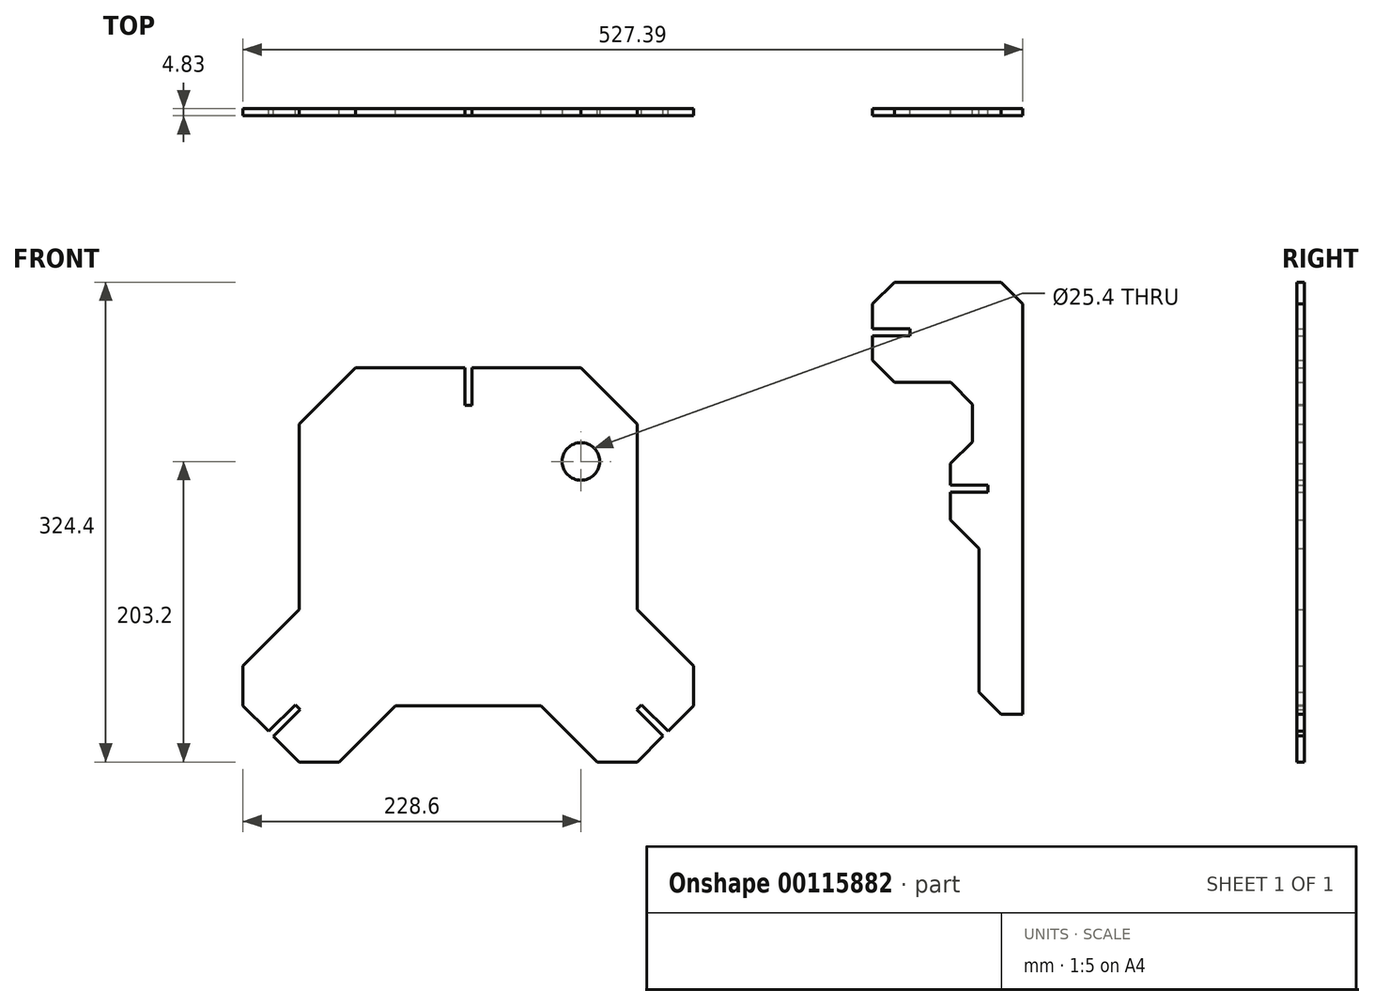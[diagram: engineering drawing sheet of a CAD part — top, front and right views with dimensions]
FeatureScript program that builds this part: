
annotation { "Feature Type Name" : "Feature", "Feature Type Description" : "" }
export const myFeature = defineFeature(function(context is Context, id is Id, definition is map)
    precondition{}
    {
        {
            var Q0;
            Q0=qCreatedBy(makeId("Front.planeOp"),FACE);
            var sketch = newSketch(context, id + "F0", { "sketchPlane" : qUnion([Q0])});
            skLineSegment(sketch, "E0.bottom", {"start": v(76.2, 133.35) * mm, "end": v(-76.2, 133.35) * mm});
            skLineSegment(sketch, "E0.top", {"start": v(114.3, -133.35) * mm, "end": v(87.36, -133.35) * mm});
            skLineSegment(sketch, "E0.left", {"start": v(114.3, 95.25) * mm, "end": v(114.3, -30.2) * mm});
            skLineSegment(sketch, "E0.right", {"start": v(-114.3, 95.25) * mm, "end": v(-114.3, -30.2) * mm});
            skPoint(sketch, "E0.middle", {"position": v(0, 0) * mm});
            skLineSegment(sketch, "E1", {"start": v(-76.2, 133.35) * mm, "end": v(-114.3, 95.25) * mm});
            skPoint(sketch, "E2.orphan", {"position": v(-114.3, 133.35) * mm});
            skLineSegment(sketch, "E3", {"start": v(76.2, 133.35) * mm, "end": v(114.3, 95.25) * mm});
            skPoint(sketch, "E4.orphan", {"position": v(114.3, 133.35) * mm});
            skLineSegment(sketch, "E5", {"start": v(114.3, -133.35) * mm, "end": v(152.4, -95.25) * mm});
            skLineSegment(sketch, "E6", {"start": v(152.4, -95.25) * mm, "end": v(152.4, -68.3) * mm});
            skLineSegment(sketch, "E7", {"start": v(152.4, -68.3) * mm, "end": v(114.3, -30.2) * mm});
            skLineSegment(sketch, "E8", {"start": v(87.36, -133.35) * mm, "end": v(49.26, -95.25) * mm});
            skPoint(sketch, "E9.orphan", {"position": v(-114.3, -133.35) * mm});
            skLineSegment(sketch, "E10", {"start": v(152.4, -68.3) * mm, "end": v(152.4, -95.25) * mm});
            skLineSegment(sketch, "E11.MirrorCS", {"start": v(-152.4, -68.3) * mm, "end": v(-114.3, -30.2) * mm});
            skLineSegment(sketch, "E12.MirrorCS", {"start": v(-114.3, -133.35) * mm, "end": v(-152.4, -95.25) * mm});
            skLineSegment(sketch, "E13.MirrorCS", {"start": v(-114.3, -133.35) * mm, "end": v(-87.36, -133.35) * mm});
            skLineSegment(sketch, "E14.MirrorCS", {"start": v(-87.36, -133.35) * mm, "end": v(-49.26, -95.25) * mm});
            skLineSegment(sketch, "E15", {"start": v(-152.4, -68.3) * mm, "end": v(-152.4, -95.25) * mm});
            skLineSegment(sketch, "E16.0", {"start": v(-49.26, -95.25) * mm, "end": v(49.26, -95.25) * mm});
            skSolve(sketch);
        }
        {
            var Q0;
            Q0=makeQuery(id+"F0.imprint","IMPRINT",FACE,{"disambiguationData":[TD([[makeQuery(id+"F0.imprint","IMPRINT",EDGE,{"derivedFrom":sQuery(id+"F0.wireOp",EDGE,"E0.bottom")}),1.0]])]});
            extrude(context, id + "F1", {"entities" : qUnion([Q0]), "depth" : 4.83 * mm});
        }
        {
            var Q0;
            Q0=qCreatedBy(makeId("Front.planeOp"),FACE);
            var sketch = newSketch(context, id + "F2", { "sketchPlane" : qUnion([Q0])});
            skLineSegment(sketch, "E17.top", {"start": v(360.2, 191.05) * mm, "end": v(288.18, 191.05) * mm});
            skLineSegment(sketch, "E18", {"start": v(288.18, 191.05) * mm, "end": v(273.4, 176.26) * mm});
            skLineSegment(sketch, "E19", {"start": v(273.4, 176.26) * mm, "end": v(273.4, 138.16) * mm});
            skPoint(sketch, "E20.orphan", {"position": v(273.4, 191.05) * mm});
            skLineSegment(sketch, "E21.trimOffspring", {"start": v(273.4, 138.16) * mm, "end": v(273.4, 176.26) * mm});
            skLineSegment(sketch, "E22", {"start": v(324.2, -98.97) * mm, "end": v(324.2, -85.44) * mm, "construction": true});
            skLineSegment(sketch, "E23.MirrorCS", {"start": v(360.2, 191.05) * mm, "end": v(375, 176.26) * mm});
            skLineSegment(sketch, "E24", {"start": v(375, 176.26) * mm, "end": v(375, -101.05) * mm});
            skPoint(sketch, "E25.orphan", {"position": v(288.17, 123.38) * mm});
            skLineSegment(sketch, "E26", {"start": v(273.4, 138.16) * mm, "end": v(288.17, 123.38) * mm});
            skPoint(sketch, "E27.start.orphan", {"position": v(273.4, -101.05) * mm});
            skPoint(sketch, "E28.orphan", {"position": v(324.2, -101.05) * mm});
            skPoint(sketch, "E29.orphan", {"position": v(375, -101.05) * mm});
            skLineSegment(sketch, "E30", {"start": v(360.2, -101.05) * mm, "end": v(375, -101.05) * mm});
            skLineSegment(sketch, "E31.0", {"start": v(360.2, 176.26) * mm, "end": v(360.2, -101.05) * mm, "construction": true});
            skLineSegment(sketch, "E32", {"start": v(360.2, -101.05) * mm, "end": v(345.43, -86.27) * mm});
            skLineSegment(sketch, "E33", {"start": v(288.17, 123.38) * mm, "end": v(326.27, 123.38) * mm});
            skLineSegment(sketch, "E34", {"start": v(326.27, 123.38) * mm, "end": v(340.83, 108.6) * mm});
            skLineSegment(sketch, "E35", {"start": v(340.83, 108.6) * mm, "end": v(340.83, 83.2) * mm});
            skLineSegment(sketch, "E36", {"start": v(340.83, 83.2) * mm, "end": v(326.05, 68.41) * mm});
            skLineSegment(sketch, "E37", {"start": v(326.05, 68.41) * mm, "end": v(326.05, 30.31) * mm});
            skLineSegment(sketch, "E38", {"start": v(326.05, 30.31) * mm, "end": v(345.43, 10.93) * mm});
            skLineSegment(sketch, "E39", {"start": v(345.43, -86.27) * mm, "end": v(345.43, 10.93) * mm});
            skPoint(sketch, "E40.orphan", {"position": v(340.83, 15.53) * mm});
            skSolve(sketch);
        }
        {
            var Q0;
            Q0 = qSketchRegion(id + "F2", true);
            extrude(context, id + "F3", {"entities" : qUnion([Q0]), "depth" : 4.83 * mm});
        }
        {
            var Q0;
            Q0=qCreatedBy(makeId("Front.planeOp"),FACE);
            var sketch = newSketch(context, id + "F4", { "sketchPlane" : qUnion([Q0])});
            skLineSegment(sketch, "E41.0", {"start": v(76.2, 133.35) * mm, "end": v(-76.2, 133.35) * mm});
            skLineSegment(sketch, "E42.0", {"start": v(-114.3, -133.35) * mm, "end": v(-152.4, -95.25) * mm});
            skLineSegment(sketch, "E43.0", {"start": v(114.3, -133.35) * mm, "end": v(152.4, -95.25) * mm});
            skLineSegment(sketch, "E44.0", {"start": v(273.4, 176.26) * mm, "end": v(273.4, 176.26) * mm});
            skPoint(sketch, "E45.middle", {"position": v(0, 133.35) * mm});
            skLineSegment(sketch, "E46", {"start": v(-133.35, -114.3) * mm, "end": v(-115.39, -96.34) * mm, "construction": true});
            skLineSegment(sketch, "E47.0", {"start": v(-131.73, -115.92) * mm, "end": v(-113.77, -97.96) * mm});
            skLineSegment(sketch, "E48.0", {"start": v(-134.97, -112.68) * mm, "end": v(-117, -94.72) * mm});
            skLineSegment(sketch, "E49", {"start": v(-117, -94.72) * mm, "end": v(-113.77, -97.96) * mm});
            skLineSegment(sketch, "E50", {"start": v(-134.97, -112.68) * mm, "end": v(-131.73, -115.92) * mm});
            skLineSegment(sketch, "E51", {"start": v(0.13, 133.35) * mm, "end": v(0.13, -121.8) * mm, "construction": true});
            skLineSegment(sketch, "E52.MirrorCS", {"start": v(117.26, -94.72) * mm, "end": v(114.03, -97.96) * mm});
            skLineSegment(sketch, "E53.MirrorCS", {"start": v(131.99, -115.92) * mm, "end": v(114.03, -97.96) * mm});
            skLineSegment(sketch, "E54.MirrorCS", {"start": v(135.22, -112.68) * mm, "end": v(117.26, -94.72) * mm});
            skLineSegment(sketch, "E55.MirrorCS", {"start": v(114.55, -133.35) * mm, "end": v(152.65, -95.25) * mm});
            skLineSegment(sketch, "E56.0", {"start": v(-2.16, 133.35) * mm, "end": v(-2.16, 107.95) * mm});
            skLineSegment(sketch, "E57.0", {"start": v(2.41, 133.35) * mm, "end": v(2.41, 107.95) * mm});
            skLineSegment(sketch, "E58", {"start": v(-2.16, 107.95) * mm, "end": v(2.41, 107.95) * mm});
            skLineSegment(sketch, "E59", {"start": v(-2.16, 133.35) * mm, "end": v(2.41, 133.35) * mm});
            skLineSegment(sketch, "E60", {"start": v(2.41, 133.35) * mm, "end": v(-2.16, 133.35) * mm});
            skLineSegment(sketch, "E61", {"start": v(273.4, 157.2) * mm, "end": v(298.8, 157.2) * mm, "construction": true});
            skLineSegment(sketch, "E62", {"start": v(326.05, 51.44) * mm, "end": v(351.45, 51.44) * mm, "construction": true});
            skLineSegment(sketch, "E63.0", {"start": v(273.4, 154.92) * mm, "end": v(298.8, 154.92) * mm});
            skLineSegment(sketch, "E64.0", {"start": v(273.4, 159.5) * mm, "end": v(298.8, 159.5) * mm});
            skLineSegment(sketch, "E65.0", {"start": v(326.05, 49.16) * mm, "end": v(351.45, 49.16) * mm});
            skLineSegment(sketch, "E66.0", {"start": v(326.05, 53.73) * mm, "end": v(351.45, 53.73) * mm});
            skLineSegment(sketch, "E67", {"start": v(298.8, 159.5) * mm, "end": v(298.8, 154.92) * mm});
            skLineSegment(sketch, "E68", {"start": v(351.45, 53.73) * mm, "end": v(351.45, 49.16) * mm});
            skLineSegment(sketch, "E69.0", {"start": v(326.05, 70.5) * mm, "end": v(326.05, 32.4) * mm});
            skLineSegment(sketch, "E70", {"start": v(273.4, 159.5) * mm, "end": v(273.4, 154.92) * mm});
            skLineSegment(sketch, "E71", {"start": v(133.6, -114.3) * mm, "end": v(108.72, -89.42) * mm, "construction": true});
            skSolve(sketch);
        }
        {
            var Q0;
            Q0 = qSketchRegion(id + "F4", true);
            extrude(context, id + "F5", {"entities" : qUnion([Q0]), "operationType" : NewBodyOperationType.REMOVE, "endBound" : BoundingType.UP_TO_NEXT, "depth" : 25.4 * mm});
        }
        {
            var Q0;
            Q0=makeQuery(id+"F1.opExtrude","CAP_FACE",FACE,{"disambiguationData":[OSD([sQuery(id+"F0.wireOp",EDGE,"E0.bottom"),sQuery(id+"F0.wireOp",EDGE,"E0.left"),sQuery(id+"F0.wireOp",EDGE,"E0.right"),sQuery(id+"F0.wireOp",EDGE,"E1"),sQuery(id+"F0.wireOp",EDGE,"E3"),sQuery(id+"F0.wireOp",EDGE,"E5"),sQuery(id+"F0.wireOp",EDGE,"E7"),sQuery(id+"F0.wireOp",EDGE,"E8"),sQuery(id+"F0.wireOp",EDGE,"E10"),sQuery(id+"F0.wireOp",EDGE,"E0.top"),sQuery(id+"F0.wireOp",EDGE,"E11.MirrorCS"),sQuery(id+"F0.wireOp",EDGE,"E12.MirrorCS"),sQuery(id+"F0.wireOp",EDGE,"E13.MirrorCS"),sQuery(id+"F0.wireOp",EDGE,"E14.MirrorCS"),sQuery(id+"F0.wireOp",EDGE,"E15"),sQuery(id+"F0.wireOp",EDGE,"E16.0")])],"isStart":false});
            var sketch = newSketch(context, id + "F6", { "sketchPlane" : qUnion([Q0])});
            skCircle(sketch, "E72", {"center": v(76.2, 69.85) * mm, "radius": 12.7 * mm});
            skSolve(sketch);
        }
        {
            var Q0;
            Q0=makeQuery(id+"F6.imprint","IMPRINT",FACE,{"disambiguationData":[TD([[makeQuery(id+"F6.imprint","IMPRINT",EDGE,{"derivedFrom":sQuery(id+"F6.wireOp",EDGE,"E72")}),1.0]])]});
            extrude(context, id + "F7", {"entities" : qUnion([Q0]), "operationType" : NewBodyOperationType.REMOVE, "endBound" : BoundingType.THROUGH_ALL, "oppositeDirection" : true, "depth" : 25.4 * mm});
        }
    });
